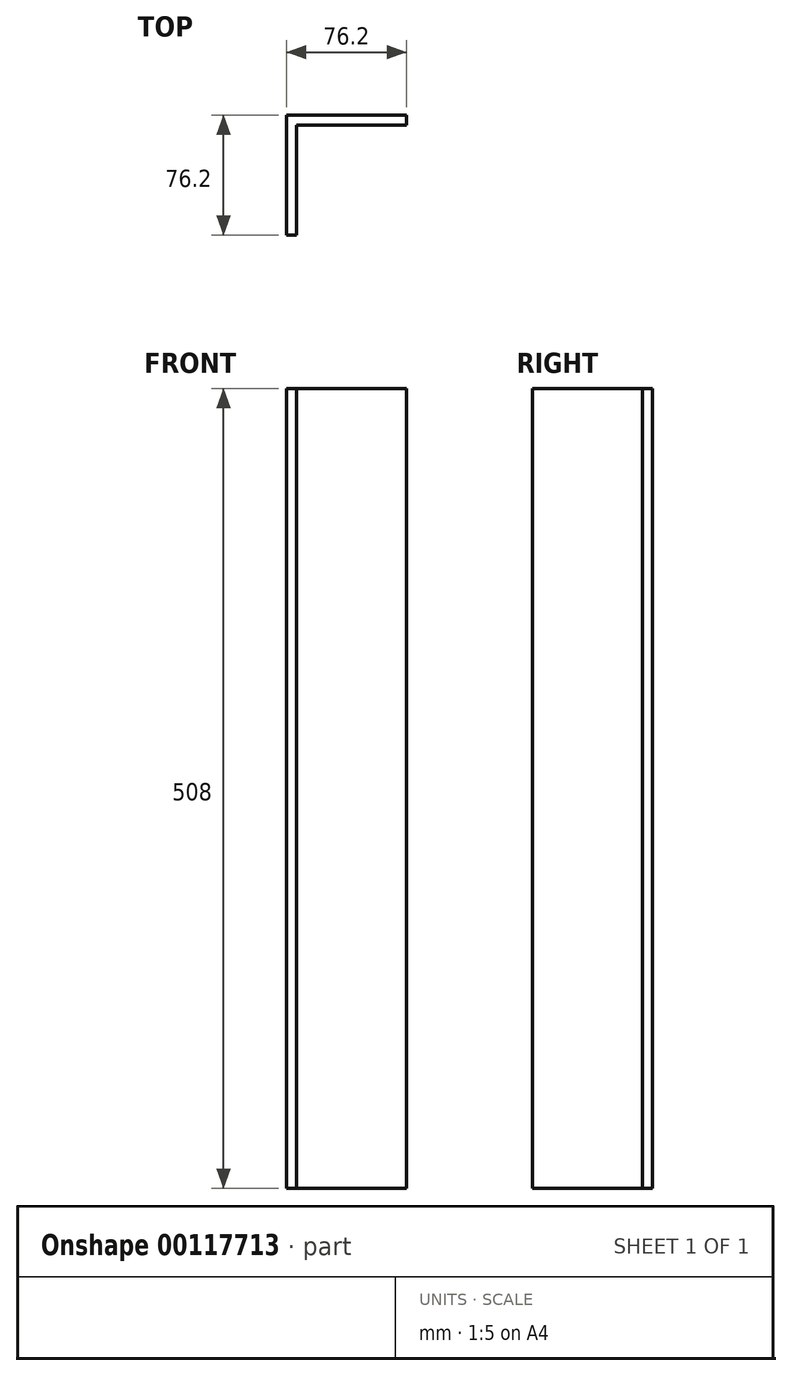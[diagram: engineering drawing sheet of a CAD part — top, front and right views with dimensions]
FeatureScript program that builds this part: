
annotation { "Feature Type Name" : "Feature", "Feature Type Description" : "" }
export const myFeature = defineFeature(function(context is Context, id is Id, definition is map)
    precondition{}
    {
        {
            var Q0;
            Q0=qCreatedBy(makeId("Top.planeOp"),FACE);
            var sketch = newSketch(context, id + "F0", { "sketchPlane" : qUnion([Q0])});
            skLineSegment(sketch, "E0", {"start": v(48.68, 27.52) * mm, "end": v(-27.52, 27.52) * mm});
            skLineSegment(sketch, "E1", {"start": v(-27.52, 27.52) * mm, "end": v(-27.52, -48.68) * mm});
            skLineSegment(sketch, "E2.0", {"start": v(-21.17, 21.17) * mm, "end": v(-21.17, -48.68) * mm});
            skLineSegment(sketch, "E2.1", {"start": v(48.68, 21.17) * mm, "end": v(-21.17, 21.17) * mm});
            skLineSegment(sketch, "E3", {"start": v(-27.52, -48.68) * mm, "end": v(-21.17, -48.68) * mm});
            skLineSegment(sketch, "E4", {"start": v(48.68, 27.52) * mm, "end": v(48.68, 21.17) * mm});
            skSolve(sketch);
        }
        {
            var Q0;
            Q0=makeQuery(id+"F0.imprint","IMPRINT",FACE,{"disambiguationData":[TD([[makeQuery(id+"F0.imprint","IMPRINT",EDGE,{"derivedFrom":sQuery(id+"F0.wireOp",EDGE,"E0")}),1.0]])]});
            extrude(context, id + "F1", {"entities" : qUnion([Q0]), "depth" : 508 * mm});
        }
    });
